# Revit family: Sanitary_Toilets_Sanindusa_Urby-Plus_Low-Level-Toilet
name_source: partatom
category: Plumbing Fixtures
revit_build: Autodesk Revit 2018 (Build: 20170223_1515(x64)
units: mm (PartAtom-declared; Revit-internal decimal feet)

## family parameters
Cut with Voids When Loaded = No
Host = Face
Part Type = Normal
Room Calculation Point = No
Round Connector Dimension = Use Diameter
Shared = No

## types (1)
- Sanitary_Toilets_Sanindusa_Urby-Plus_Low-Level-Toilet
    AssetType = Fixed
    CodePerformance = EN 997:2012 CL 1 - 6 A
    Color = white
    Constituents = Compatible toilet seats (not included): 2401100-Urby toilet seat with clipoff system; 24031-Urby toilet seat with clipoff and slowclose system.
    Default Elevation = 1219 mm
    Description = Soil appliance for the disposal of excrement.
    DrainSize = 90 mm  [stored 0.295276 ft]
    Element Type = TOILETPAN: Soil appliance for the disposal of excrement.
    Features = Domestic and commercial use. Versatile timeless design. Seats with clipoff system easy to clean and slow close option. Back to wall WC.
    Finish = gloss
    Installation Instructions = https://www.tec.sanindusa.pt
    InstallationDate = 1900-12-31T23:59:59
    Manufacturer = Sanindusa
    ManufacturerName = Sanindusa
    ManufacturerURL = www.tec.sanindusa.pt
    Material = vitreous china
    Model = 146011004
    ModelNumber = 146011004
    ModelReference = Urby Plus
    Name = urb.y plus F|D low level toilet
    NominalHeight = 400 mm  [stored 1.31234 ft]
    NominalLength = 355 mm
    NominalWidth = 405 mm
    PanColor = white
    PanMaterial = vitreous china
    PanMounting = backtowall
    Pre-defined type (IFC) = TOILETPAN
    ProductInformation = https://www.tec.sanindusa.pt
    ProductionYear = 2019
    Size = 355x405x400
    ToiletPanType = siphonic
    ToiletType = LooseCoupled
    Type (IFC) = IfcSanitaryTerminalType
    URL = www.tec.sanindusa.pt
    Uniclass2015Code = Pr_40_20_93_94
    Uniclass2015Title = WC pans
    Uniclass2015Version = Products v1.6
    Version = 1
    WarrantyDescription = https://www.tec.sanindusa.pt
    WarrantyDurationParts = 5
    WarrantyDurationUnit = year
    WarrantyStartDate = 1900-12-31T23:59:59
    Waste Connection = Yes
    Weight = 32.10 kg

note: [stored X ft] marks values corroborated as IEEE doubles in the binary element streams (Revit-internal decimal feet)

## geometry (parser evidence)
native form markers: Sweep x7
no freeform markers — native parametric forms only
